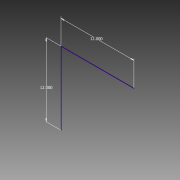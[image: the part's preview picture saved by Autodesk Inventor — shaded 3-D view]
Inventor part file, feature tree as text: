
AUTODESK INVENTOR PART (.ipt)
format: ipt  version: 2013 (Build 170138000, 138)  size: 58,880 bytes
history: native  units: in
note: dims shown in document units (in); Inventor stores cm internally (conversion verified against a paired STEP export)
features: sketch x1
ambient origin geometry x8: Origin, YZ Plane, XZ Plane, XY Plane, X Axis, Y Axis, Z Axis, Center Point
feature tree (1):
  sketch  "Sketch1"  dims[d0=12.0in d1=12.0in]
